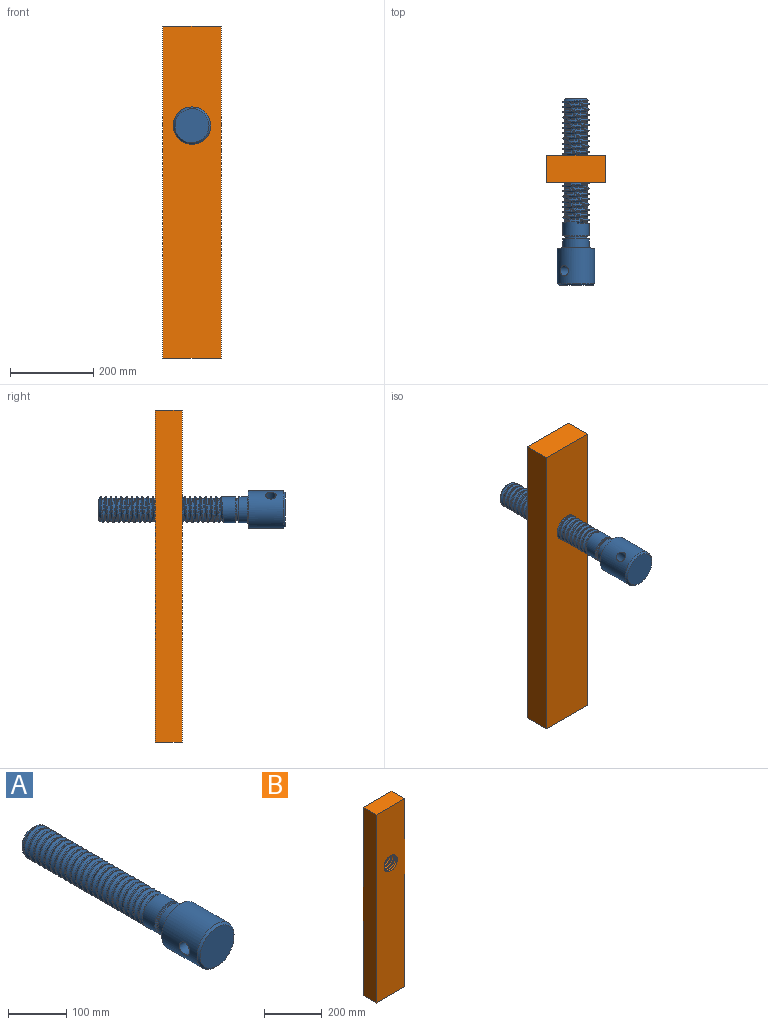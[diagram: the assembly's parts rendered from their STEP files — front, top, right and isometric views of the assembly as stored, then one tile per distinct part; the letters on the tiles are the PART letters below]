
ASSEMBLY  parts=2 mates=1
PART A: 44 faces, bbox 90.3x452x90.3 mm
  f0: cylinder r=45mm len=90mm, axis (0,-1,0), area 23323.3mm2, adj f37,f39,f43
  f1: cylinder r=31.5mm len=63mm, axis (0,-1,0), area 6155.5mm2, adj f2,f27,f29,f31,f32,f33
  f2: cylinder r=31.5mm len=63mm, axis (0,-1,0), area 313.8mm2, adj f1,f3,f29,f31
  f3: cylinder r=31.5mm len=63mm, axis (0,-1,0), area 314.4mm2, adj f2,f4,f29,f31
  f4: cylinder r=31.5mm len=63mm, axis (0,-1,0), area 314.3mm2, adj f3,f5,f29,f31
  f5: cylinder r=31.5mm len=63mm, axis (0,-1,0), area 314.8mm2, adj f4,f6,f29,f31
  f6: cylinder r=31.5mm len=63mm, axis (0,-1,0), area 314.8mm2, adj f5,f7,f29,f31
  f7: cylinder r=31.5mm len=63mm, axis (0,-1,0), area 313.7mm2, adj f6,f8,f29,f31
  f8: cylinder r=31.5mm len=63mm, axis (0,-1,0), area 313.9mm2, adj f7,f9,f29,f31
  f9: cylinder r=31.5mm len=63mm, axis (0,-1,0), area 314.5mm2, adj f8,f10,f29,f31
  f10: cylinder r=31.5mm len=63mm, axis (0,-1,0), area 314.3mm2, adj f9,f11,f29,f31
  f11: cylinder r=31.5mm len=63mm, axis (0,-1,0), area 314.3mm2, adj f10,f12,f29,f31
  f12: cylinder r=31.5mm len=63mm, axis (0,-1,0), area 314.8mm2, adj f11,f13,f29,f31
  f13: cylinder r=31.5mm len=63mm, axis (0,-1,0), area 315.1mm2, adj f12,f14,f29,f31
  f14: cylinder r=31.5mm len=63mm, axis (0,-1,0), area 313.9mm2, adj f13,f15,f29,f31
  f15: cylinder r=31.5mm len=63mm, axis (0,-1,0), area 313.8mm2, adj f14,f16,f29,f31
  f16: cylinder r=31.5mm len=63mm, axis (0,-1,0), area 314.4mm2, adj f15,f17,f29,f31
  f17: cylinder r=31.5mm len=63mm, axis (0,-1,0), area 314.3mm2, adj f16,f18,f29,f31
  f18: cylinder r=31.5mm len=63mm, axis (0,-1,0), area 314.2mm2, adj f17,f19,f29,f31
  f19: cylinder r=31.5mm len=63mm, axis (0,-1,0), area 314.7mm2, adj f18,f20,f29,f31
  f20: cylinder r=31.5mm len=63mm, axis (0,-1,0), area 315.3mm2, adj f19,f21,f29,f31
  f21: cylinder r=31.5mm len=63mm, axis (0,-1,0), area 314.2mm2, adj f20,f22,f29,f31
  f22: cylinder r=31.5mm len=63mm, axis (0,-1,0), area 313.8mm2, adj f21,f23,f29,f31
  f23: cylinder r=31.5mm len=63mm, axis (0,-1,0), area 314.2mm2, adj f22,f24,f29,f31
  f24: cylinder r=31.5mm len=63mm, axis (0,-1,0), area 233.7mm2, adj f23,f26,f28,f29,f31
  f25: plane 50.3x50.3mm, normal (0,1,0), area 1987.1mm2, adj f26
  f26: cone r=31.5mm half-angle=45deg, axis (0,-1,0), area 1123.1mm2, adj f24,f25,f28,f30,f31
  f27: plane 3.21x2.31mm, normal (-0.72,0,-0.69), area 5.2mm2, adj f1,f31,f32
  f28: plane 6.2x4.72mm, normal (-1,0,0), area 7mm2, adj f24,f26,f29,f30
  f29: bspline ~300.83x63.47mm, area 24052mm2, adj f1,f2,f3,f4,f5,f6,f7,f8
  f30: bspline ~303.21x55.48mm, area 14041.5mm2, adj f26,f28,f29,f31,f32
  f31: bspline ~302.42x63.47mm, area 24137.8mm2, adj f1,f2,f3,f4,f5,f6,f7,f8
  f32: plane 63.32x53.68mm, normal (0,1,0), area 360.8mm2, adj f1,f27,f29,f30,f31
  f33: plane 63x63mm, normal (0,-1,0), area 654.2mm2, adj f1,f40
  f34: cylinder r=26.5mm len=53mm, axis (0,-1,0), area 832.5mm2, adj f40,f41
  f35: plane 63x63mm, normal (0,1,0), area 654.2mm2, adj f36,f41
  f36: cylinder r=31.5mm len=63mm, axis (0,-1,0), area 4057.4mm2, adj f35,f42
  f37: plane 90x90mm, normal (0,1,0), area 2940.5mm2, adj f0,f42
  f38: plane 82x82mm, normal (0,-1,0), area 5281mm2, adj f43
  f39: cylinder r=12.5mm len=86.46mm, axis (-1,0,0), area 6790.4mm2, adj f0
  f40: torus R=28mm, axis (0,1,0), area 400.4mm2, adj f33,f34
  f41: torus R=28mm, axis (0,-1,0), area 400.4mm2, adj f34,f35
  f42: torus R=33mm, axis (0,-1,0), area 474.4mm2, adj f36,f37
  f43: cone r=41mm half-angle=45deg, axis (0,1,0), area 1528.4mm2, adj f0,f38
PART B: 12 faces, bbox 140x71.4x800 mm
  f0: plane 800x140mm, normal (0,1,0), area 108603.3mm2, adj f2,f3,f4,f5,f7
  f1: plane 800x140mm, normal (0,-1,0), area 108603.3mm2, adj f2,f3,f4,f5,f6
  f2: plane 800x65mm, normal (-1,0,0), area 52000mm2, adj f0,f1,f3,f4
  f3: plane 140x65mm, normal (0,0,-1), area 9100mm2, adj f0,f1,f2,f5
  f4: plane 140x65mm, normal (0,0,1), area 9100mm2, adj f0,f1,f2,f5
  f5: plane 800x65mm, normal (1,0,0), area 52000mm2, adj f0,f1,f3,f4
  f6: cone r=27.88mm half-angle=45deg, axis (0,-1,0), area 896.7mm2, adj f1,f8,f9,f10,f11
  f7: cone r=32.88mm half-angle=45deg, axis (0,1,0), area 896.9mm2, adj f0,f8,f9,f10,f11
  f8: bspline ~66.68x64.63mm, area 1747.3mm2, adj f6,f7,f9,f10
  f9: bspline ~67.47x63.7mm, area 4904mm2, adj f6,f7,f8,f11
  f10: bspline ~67.47x63.7mm, area 4860.1mm2, adj f6,f7,f8,f11
  f11: cylinder r=27.88mm len=55.76mm, axis (0,1,0), area 2413.5mm2, adj f6,f7,f9,f10
PLACE A rot(axis=(0,-1,0),129.9deg) t=(-386.83,-158.7,156.65)mm
PLACE B t=(-386.83,22.11,-3.35)mm fixed
MATE cylindrical B.f6 <-> A.f1  axis (0,-1,0) through (-386.83,-60.39,156.65)mm
